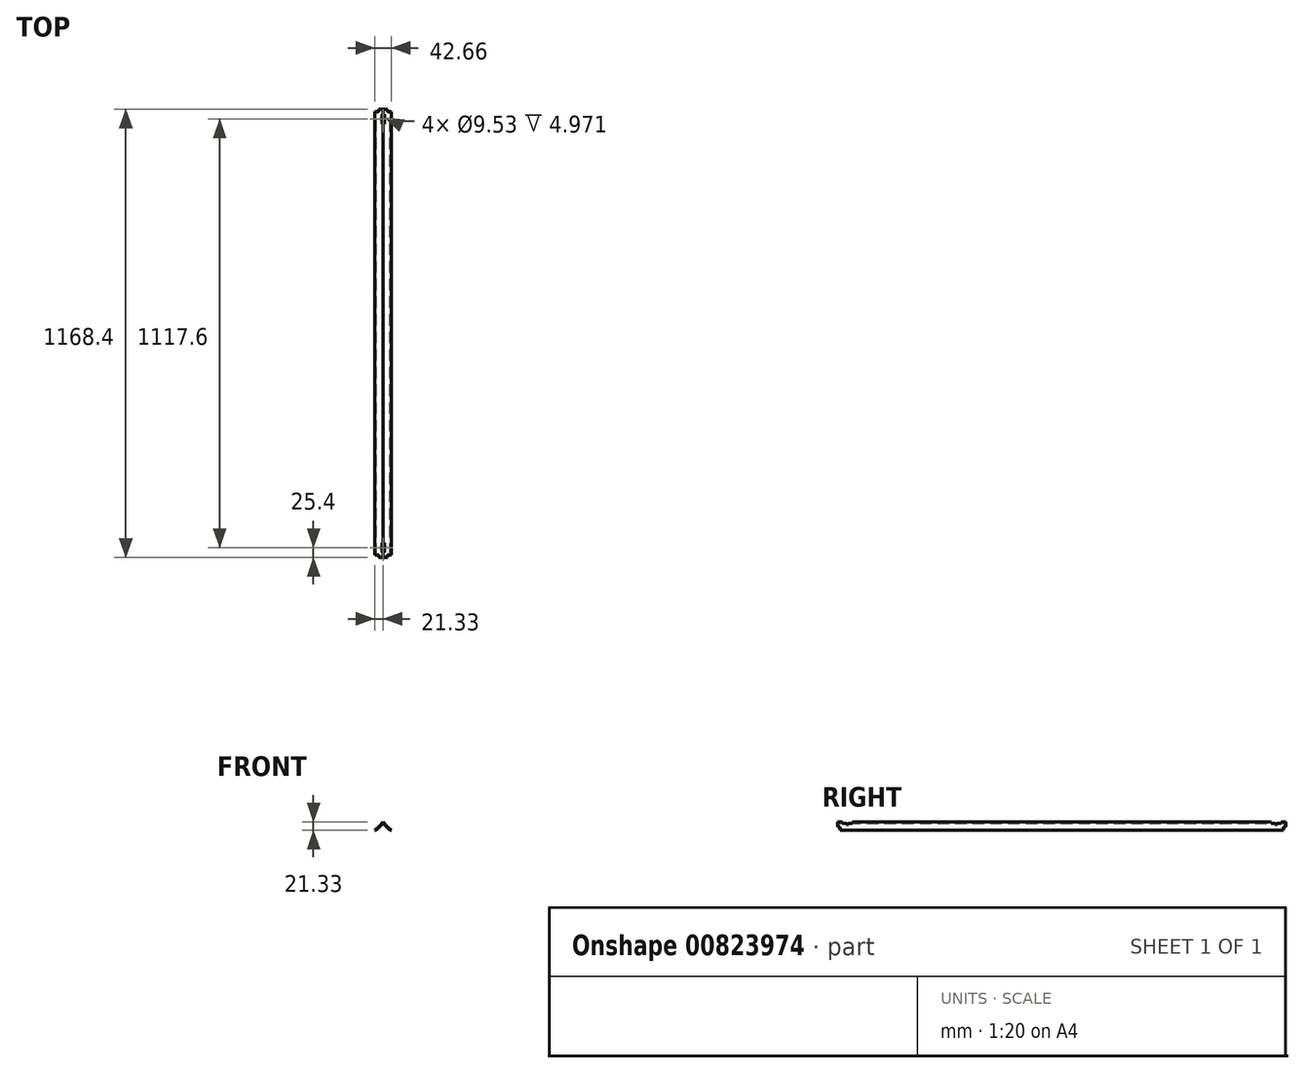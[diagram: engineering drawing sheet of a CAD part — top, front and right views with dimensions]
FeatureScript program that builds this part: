
annotation { "Feature Type Name" : "Feature", "Feature Type Description" : "" }
export const myFeature = defineFeature(function(context is Context, id is Id, definition is map)
    precondition{}
    {
        {
            var Q0;
            Q0=qCreatedBy(makeId("Front.planeOp"),FACE);
            var sketch = newSketch(context, id + "F0", { "sketchPlane" : qUnion([Q0])});
            skLineSegment(sketch, "E0.top", {"start": v(21.33, 0) * mm, "end": v(0, 21.33) * mm});
            skLineSegment(sketch, "E0.right", {"start": v(-21.33, 0) * mm, "end": v(0, 21.33) * mm});
            skPoint(sketch, "E0.middle", {"position": v(0, 0) * mm});
            skLineSegment(sketch, "E1", {"start": v(-17.96, 0) * mm, "end": v(0, 17.96) * mm});
            skLineSegment(sketch, "E2", {"start": v(0, 17.96) * mm, "end": v(17.96, 0) * mm});
            skLineSegment(sketch, "E3", {"start": v(21.33, 0) * mm, "end": v(17.96, 0) * mm});
            skLineSegment(sketch, "E4", {"start": v(-21.33, 0) * mm, "end": v(-17.96, 0) * mm});
            skSolve(sketch);
        }
        {
            var Q0;
            Q0=makeQuery(id+"F0.imprint","IMPRINT",FACE,{"disambiguationData":[TD([[makeQuery(id+"F0.imprint","IMPRINT",EDGE,{"derivedFrom":sQuery(id+"F0.wireOp",EDGE,"E0.top")}),1.0]])]});
            extrude(context, id + "F1", {"entities" : qUnion([Q0]), "endBound" : BoundingType.SYMMETRIC, "depth" : 1168.4 * mm, "offsetDistance" : 25.4 * mm});
        }
        {
            var Q0;
            Q0=qCreatedBy(makeId("Right.planeOp"),FACE);
            cPlane(context, id + "F2", {"entities" : qUnion([Q0]), "cplaneType" : CPlaneType.OFFSET, "offset" : 37.6 * mm, "width" : 152.4 * mm, "height" : 152.4 * mm});
        }
        {
            var Q0;
            Q0=qCreatedBy(id+"F2.planeOp",FACE);
            var sketch = newSketch(context, id + "F3", { "sketchPlane" : qUnion([Q0])});
            skLineSegment(sketch, "E5.bottom", {"start": v(-571.5, 21.33) * mm, "end": v(-546.1, 21.33) * mm});
            skLineSegment(sketch, "E5.top", {"start": v(-571.5, 18.15) * mm, "end": v(-546.1, 18.15) * mm});
            skLineSegment(sketch, "E5.left", {"start": v(-571.5, 21.33) * mm, "end": v(-571.5, 18.15) * mm});
            skLineSegment(sketch, "E5.right", {"start": v(-546.1, 21.33) * mm, "end": v(-546.1, 18.15) * mm});
            skLineSegment(sketch, "E6.MirrorCS", {"start": v(571.5, 18.15) * mm, "end": v(546.1, 18.15) * mm});
            skLineSegment(sketch, "E7.MirrorCS", {"start": v(546.1, 21.33) * mm, "end": v(546.1, 18.15) * mm});
            skLineSegment(sketch, "E8.MirrorCS", {"start": v(571.5, 21.33) * mm, "end": v(546.1, 21.33) * mm});
            skLineSegment(sketch, "E9.MirrorCS", {"start": v(571.5, 21.33) * mm, "end": v(571.5, 18.15) * mm});
            skLineSegment(sketch, "E10", {"start": v(-558.8, 18.15) * mm, "end": v(-558.8, 21.33) * mm, "construction": true});
            skLineSegment(sketch, "E11.MirrorCS", {"start": v(558.8, 18.15) * mm, "end": v(558.8, 21.33) * mm, "construction": true});
            skLineSegment(sketch, "E12.bottom", {"start": v(-584.2, 0) * mm, "end": v(-577.85, 0) * mm});
            skLineSegment(sketch, "E12.top", {"start": v(-584.2, 9.53) * mm, "end": v(-577.85, 9.53) * mm});
            skLineSegment(sketch, "E12.left", {"start": v(-584.2, 0) * mm, "end": v(-584.2, 9.53) * mm});
            skLineSegment(sketch, "E12.right", {"start": v(-577.85, 0) * mm, "end": v(-577.85, 9.53) * mm});
            skLineSegment(sketch, "E13.MirrorCS", {"start": v(584.2, 9.53) * mm, "end": v(577.85, 9.53) * mm});
            skLineSegment(sketch, "E14.MirrorCS", {"start": v(577.85, 0) * mm, "end": v(577.85, 9.53) * mm});
            skLineSegment(sketch, "E15.MirrorCS", {"start": v(584.2, 0) * mm, "end": v(577.85, 0) * mm});
            skLineSegment(sketch, "E16.MirrorCS", {"start": v(584.2, 0) * mm, "end": v(584.2, 9.53) * mm});
            skSolve(sketch);
        }
        {
            var Q0;
            Q0=makeQuery(id+"F3.imprint","IMPRINT",FACE,{"disambiguationData":[TD([[makeQuery(id+"F3.imprint","IMPRINT",EDGE,{"derivedFrom":sQuery(id+"F3.wireOp",EDGE,"E5.bottom")}),-1.0]])]});
            var Q1;
            Q1=makeQuery(id+"F3.imprint","IMPRINT",FACE,{"disambiguationData":[TD([[makeQuery(id+"F3.imprint","IMPRINT",EDGE,{"derivedFrom":sQuery(id+"F3.wireOp",EDGE,"E6.MirrorCS")}),-1.0]])]});
            var Q2;
            Q2=makeQuery(id+"F3.imprint","IMPRINT",FACE,{"disambiguationData":[TD([[makeQuery(id+"F3.imprint","IMPRINT",EDGE,{"derivedFrom":sQuery(id+"F3.wireOp",EDGE,"E13.MirrorCS")}),1.0]])]});
            var Q3;
            Q3=makeQuery(id+"F3.imprint","IMPRINT",FACE,{"disambiguationData":[TD([[makeQuery(id+"F3.imprint","IMPRINT",EDGE,{"derivedFrom":sQuery(id+"F3.wireOp",EDGE,"E12.bottom")}),1.0]])]});
            extrude(context, id + "F4", {"entities" : qUnion([Q0, Q1, Q2, Q3]), "operationType" : NewBodyOperationType.REMOVE, "oppositeDirection" : true, "depth" : 68.58 * mm, "offsetDistance" : 25.4 * mm});
        }
        {
            var Q0;
            Q0=makeQuery(id+"F4.boolean.opBoolean","COPY",FACE,{"derivedFrom":makeQuery(id+"F4.opExtrude","SWEPT_FACE",FACE,{"disambiguationData":[OSD([sQuery(id+"F3.wireOp",EDGE,"E5.top")])]})});
            var sketch = newSketch(context, id + "F5", { "sketchPlane" : qUnion([Q0])});
            skCircle(sketch, "E17", {"center": v(0, -558.8) * mm, "radius": 4.76 * mm});
            skPoint(sketch, "E17.centerSnap0", {"position": v(-3.18, -558.8) * mm});
            skCircle(sketch, "E18.MirrorC", {"center": v(0, 558.8) * mm, "radius": 4.76 * mm});
            skSolve(sketch);
        }
        {
            var Q0;
            Q0=sQuery(id+"F5.wireOp",VERTEX,"E17.center");
            var Q1;
            Q1=sQuery(id+"F5.wireOp",VERTEX,"E18.MirrorC.center");
            var Q2;
            Q2=makeQuery(id+"F1.opExtrude","SWEPT_BODY",BODY,{"disambiguationData":[OSD([sQuery(id+"F0.wireOp",EDGE,"E0.bottom"),sQuery(id+"F0.wireOp",EDGE,"E0.top"),sQuery(id+"F0.wireOp",EDGE,"E0.left"),sQuery(id+"F0.wireOp",EDGE,"E0.right"),sQuery(id+"F0.wireOp",EDGE,"E1"),sQuery(id+"F0.wireOp",EDGE,"E2")])]});
            hole(context, id + "F6", {"style" : HoleStyle.SIMPLE, "endStyle" : HoleEndStyle.THROUGH, "holeDiameter" : 9.52 * mm, "majorDiameter" : 6.35 * mm, "isTappedThrough" : true, "tappedDepth" : 12.7 * mm, "tapClearance" : 3, "locations" : qUnion([Q0, Q1]), "scope" : qUnion([Q2])});
        }
    });
